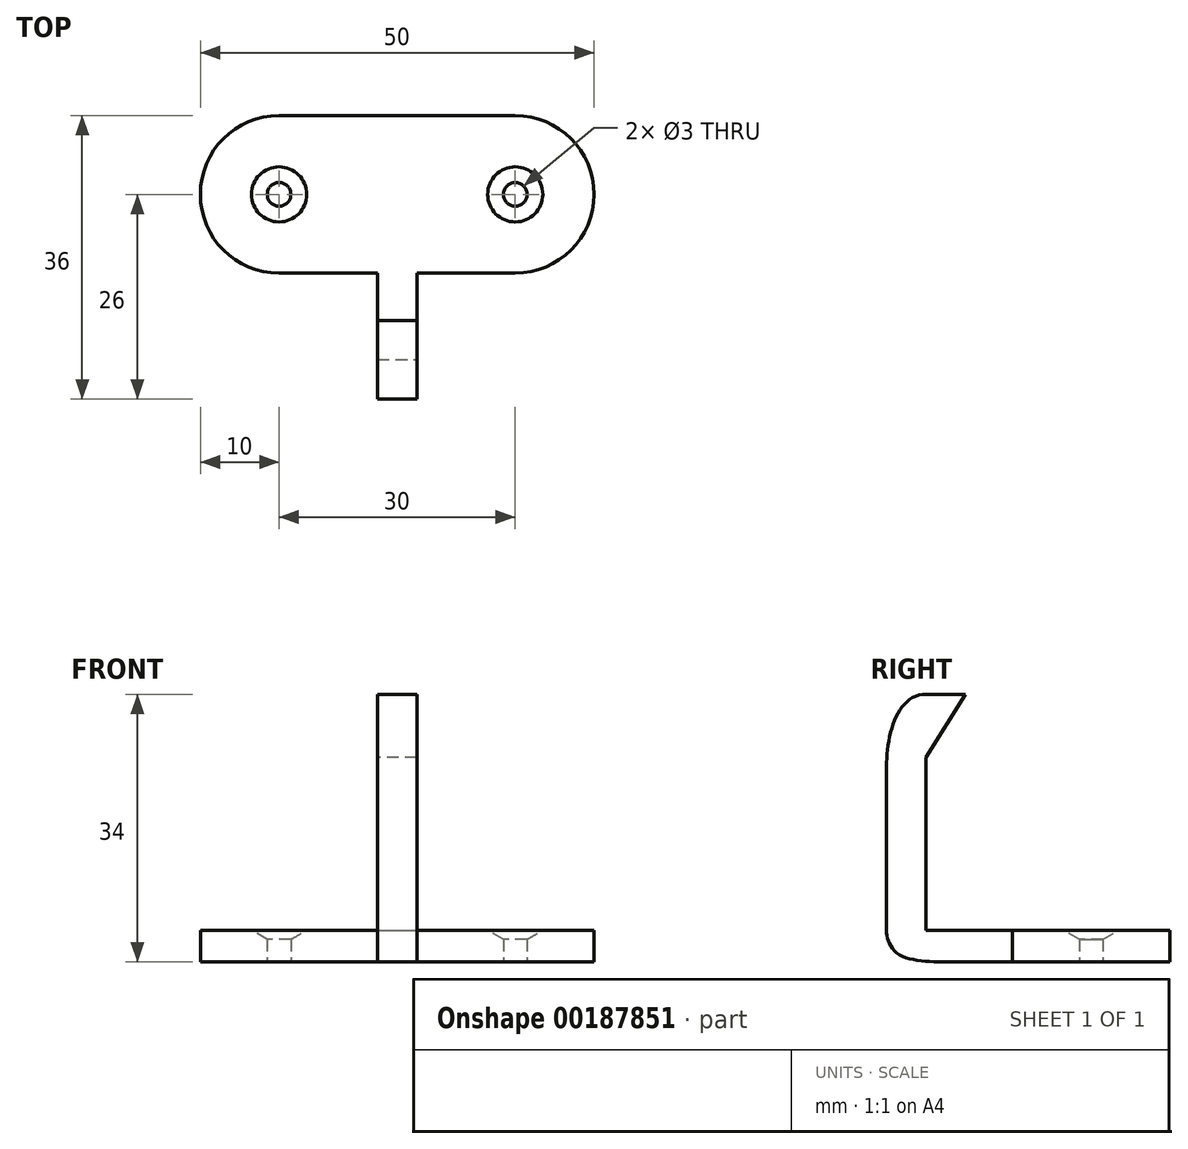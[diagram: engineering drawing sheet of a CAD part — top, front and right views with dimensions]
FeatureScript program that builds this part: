
annotation { "Feature Type Name" : "Feature", "Feature Type Description" : "" }
export const myFeature = defineFeature(function(context is Context, id is Id, definition is map)
    precondition{}
    {
        {
            var Q0;
            Q0=qCreatedBy(makeId("Top.planeOp"),FACE);
            var sketch = newSketch(context, id + "F0", { "sketchPlane" : qUnion([Q0])});
            skLineSegment(sketch, "E0.bottom", {"start": v(-15, 10) * mm, "end": v(15, 10) * mm});
            skLineSegment(sketch, "E0.top", {"start": v(-15, -10) * mm, "end": v(15, -10) * mm});
            skArc(sketch, "E1", {"start": v(-15, 10) * mm, "mid": v(-25, 0) * mm, "end": v(-15, -10) * mm});
            skArc(sketch, "E2", {"start": v(15, -10) * mm, "mid": v(25, 0) * mm, "end": v(15, 10) * mm});
            skPoint(sketch, "E2.centerSnap0", {"position": v(15, 0) * mm});
            skCircle(sketch, "E3", {"center": v(-15, 0) * mm, "radius": 1.5 * mm});
            skCircle(sketch, "E4", {"center": v(15, 0) * mm, "radius": 1.5 * mm});
            skSolve(sketch);
        }
        {
            var Q0;
            Q0=makeQuery(id+"F0.imprint","IMPRINT",FACE,{"disambiguationData":[TD([[makeQuery(id+"F0.imprint","IMPRINT",EDGE,{"derivedFrom":sQuery(id+"F0.wireOp",EDGE,"E0.bottom")}),-1.0]])]});
            extrude(context, id + "F1", {"entities" : qUnion([Q0]), "depth" : 4 * mm});
        }
        {
            var Q0;
            Q0=qCreatedBy(makeId("Right.planeOp"),FACE);
            var sketch = newSketch(context, id + "F2", { "sketchPlane" : qUnion([Q0])});
            skLineSegment(sketch, "E5.bottom", {"start": v(10, 4) * mm, "end": v(-10, 4) * mm});
            skLineSegment(sketch, "E5.top", {"start": v(10, 0) * mm, "end": v(-10, 0) * mm});
            skLineSegment(sketch, "E5.left", {"start": v(10, 4) * mm, "end": v(10, 0) * mm});
            skLineSegment(sketch, "E5.right", {"start": v(-10, 4) * mm, "end": v(-10, 0) * mm});
            skLineSegment(sketch, "E6.bottom", {"start": v(-10, 4) * mm, "end": v(-26, 4) * mm});
            skLineSegment(sketch, "E6.top", {"start": v(-10, 0) * mm, "end": v(-18, 0) * mm});
            skLineSegment(sketch, "E6.right", {"start": v(-26, 4) * mm, "end": v(-26, 3) * mm});
            skFitSpline(sketch, "E7", {"points": [v(-26, 4) * mm, v(-24.52, 1) * mm, v(-18, 0) * mm], "startDerivative": vector(0, -7.21) * mm, "endDerivative": vector(10.27, 0) * mm});
            skPoint(sketch, "E8.orphan", {"position": v(-26, 0) * mm});
            skSolve(sketch);
        }
        {
            var Q0;
            Q0=makeQuery(id+"F2.imprint","IMPRINT",FACE,{"disambiguationData":[TD([[makeQuery(id+"F2.imprint","IMPRINT",EDGE,{"derivedFrom":sQuery(id+"F2.wireOp",EDGE,"E6.bottom")}),1.0]])]});
            extrude(context, id + "F3", {"entities" : qUnion([Q0]), "operationType" : NewBodyOperationType.ADD, "endBound" : BoundingType.SYMMETRIC, "depth" : 5 * mm});
        }
        {
            var Q0;
            Q0=makeQuery(id+"F3.boolean.opBoolean","MERGE",FACE,{"derivedFrom":[makeQuery(id+"F1.opExtrude","CAP_FACE",FACE,{"disambiguationData":[OSD([sQuery(id+"F0.wireOp",EDGE,"E0.bottom"),sQuery(id+"F0.wireOp",EDGE,"E0.top"),sQuery(id+"F0.wireOp",EDGE,"E1"),sQuery(id+"F0.wireOp",EDGE,"E2"),sQuery(id+"F0.wireOp",EDGE,"E3"),sQuery(id+"F0.wireOp",EDGE,"E4")])],"isStart":false}),makeQuery(id+"F3.opExtrude","SWEPT_FACE",FACE,{"disambiguationData":[OSD([sQuery(id+"F2.wireOp",EDGE,"E6.bottom")])]})]});
            var sketch = newSketch(context, id + "F4", { "sketchPlane" : qUnion([Q0])});
            skLineSegment(sketch, "E9.bottom", {"start": v(-2.5, -26) * mm, "end": v(2.5, -26) * mm});
            skLineSegment(sketch, "E9.top", {"start": v(-2.5, -21) * mm, "end": v(2.5, -21) * mm});
            skLineSegment(sketch, "E9.left", {"start": v(-2.5, -26) * mm, "end": v(-2.5, -21) * mm});
            skLineSegment(sketch, "E9.right", {"start": v(2.5, -26) * mm, "end": v(2.5, -21) * mm});
            skSolve(sketch);
        }
        {
            var Q0;
            Q0=makeQuery(id+"F4.imprint","IMPRINT",FACE,{"disambiguationData":[TD([[makeQuery(id+"F4.imprint","IMPRINT",EDGE,{"derivedFrom":sQuery(id+"F4.wireOp",EDGE,"E9.bottom")}),-1.0]])]});
            extrude(context, id + "F5", {"entities" : qUnion([Q0]), "operationType" : NewBodyOperationType.ADD, "depth" : 30 * mm});
        }
        {
            var Q0;
            Q0=makeQuery(id+"F5.boolean.opBoolean","MERGE",FACE,{"derivedFrom":[makeQuery(id+"F3.opExtrude","CAP_FACE",FACE,{"disambiguationData":[OSD([sQuery(id+"F2.wireOp",EDGE,"E6.bottom"),sQuery(id+"F2.wireOp",EDGE,"E6.top"),sQuery(id+"F2.wireOp",EDGE,"E5.right"),sQuery(id+"F2.wireOp",EDGE,"E7")])],"isStart":true}),makeQuery(id+"F5.opExtrude","SWEPT_FACE",FACE,{"disambiguationData":[OSD([sQuery(id+"F4.wireOp",EDGE,"E9.left")])]})]});
            var sketch = newSketch(context, id + "F6", { "sketchPlane" : qUnion([Q0])});
            skFitSpline(sketch, "E10", {"points": [v(26, 24.79) * mm, v(21, 34) * mm], "startDerivative": vector(0, 11.97) * mm, "endDerivative": vector(-11.06, 0) * mm});
            skLineSegment(sketch, "E11", {"start": v(21, 34) * mm, "end": v(16, 34) * mm});
            skLineSegment(sketch, "E12", {"start": v(16, 34) * mm, "end": v(21, 26) * mm});
            skLineSegment(sketch, "E13", {"start": v(21, 26) * mm, "end": v(21, 34) * mm});
            skSolve(sketch);
        }
        {
            var Q0;
            {var subQ0=sQuery(id+"F6.wireOp",EDGE,"E10");Q0=makeQuery(id+"F6.imprint","IMPRINT",FACE,{"disambiguationData":[TD([[makeQuery(id+"F6.imprint","IMPRINT",EDGE,{"derivedFrom":subQ0}),-1.0]])]});}
            extrude(context, id + "F7", {"entities" : qUnion([Q0]), "operationType" : NewBodyOperationType.REMOVE, "endBound" : BoundingType.UP_TO_NEXT, "oppositeDirection" : true, "depth" : 25 * mm});
        }
        {
            var Q0;
            Q0=qCreatedBy(makeId("Right.planeOp"),FACE);
            var Q1;
            Q1=sQuery(id+"F0.wireOp",VERTEX,"E2.centerSnap0");
            cPlane(context, id + "F8", {"entities" : qUnion([Q0, Q1]), "cplaneType" : CPlaneType.PLANE_POINT, "offset" : 16 * mm, "width" : 150 * mm, "height" : 150 * mm});
        }
        {
            var Q0;
            Q0=qCreatedBy(id+"F8.planeOp",FACE);
            var sketch = newSketch(context, id + "F9", { "sketchPlane" : qUnion([Q0])});
            skLineSegment(sketch, "E14", {"start": v(0, 0) * mm, "end": v(0, 4) * mm, "construction": true});
            skLineSegment(sketch, "E15", {"start": v(0, 4) * mm, "end": v(3.5, 4) * mm});
            skLineSegment(sketch, "E16", {"start": v(0, 4) * mm, "end": v(-3.5, 4) * mm, "construction": true});
            skLineSegment(sketch, "E17", {"start": v(0, 2) * mm, "end": v(3.5, 4) * mm});
            skLineSegment(sketch, "E18", {"start": v(0, 4) * mm, "end": v(0, 2) * mm});
            skSolve(sketch);
        }
        {
            var Q0;
            Q0=makeQuery(id+"F9.imprint","IMPRINT",FACE,{"disambiguationData":[TD([[makeQuery(id+"F9.imprint","IMPRINT",EDGE,{"derivedFrom":sQuery(id+"F9.wireOp",EDGE,"E15")}),-1.0]])]});
            var Q1;
            Q1=sQuery(id+"F9.wireOp",EDGE,"E18");
            revolve(context, id + "F10", {"operationType" : NewBodyOperationType.REMOVE, "entities" : qUnion([Q0]), "axis" : qUnion([Q1]), "revolveType" : RevolveType.FULL, "oppositeDirection" : true});
        }
        {
            var Q0;
            Q0=sQuery(id+"F0.wireOp",VERTEX,"E1.center");
            var Q1;
            Q1=qCreatedBy(makeId("Right.planeOp"),FACE);
            cPlane(context, id + "F11", {"entities" : qUnion([Q0, Q1]), "cplaneType" : CPlaneType.PLANE_POINT, "offset" : 25 * mm, "width" : 150 * mm, "height" : 150 * mm});
        }
        {
            var Q0;
            Q0=qCreatedBy(id+"F11.planeOp",FACE);
            var sketch = newSketch(context, id + "F12", { "sketchPlane" : qUnion([Q0])});
            skLineSegment(sketch, "E19", {"start": v(0, 0) * mm, "end": v(0, 4) * mm, "construction": true});
            skLineSegment(sketch, "E20", {"start": v(0, 4) * mm, "end": v(3.5, 4) * mm});
            skLineSegment(sketch, "E21", {"start": v(0, 4) * mm, "end": v(-3.5, 4) * mm, "construction": true});
            skLineSegment(sketch, "E22", {"start": v(0, 2) * mm, "end": v(3.5, 4) * mm});
            skLineSegment(sketch, "E23", {"start": v(0, 4) * mm, "end": v(0, 2) * mm});
            skSolve(sketch);
        }
        {
            var Q0;
            Q0=makeQuery(id+"F12.imprint","IMPRINT",FACE,{"disambiguationData":[TD([[makeQuery(id+"F12.imprint","IMPRINT",EDGE,{"derivedFrom":sQuery(id+"F12.wireOp",EDGE,"E20")}),-1.0]])]});
            var Q1;
            Q1=makeQuery(id+"F1.opExtrude","SWEPT_FACE",FACE,{"disambiguationData":[OSD([sQuery(id+"F0.wireOp",EDGE,"E1")])]});
            revolve(context, id + "F13", {"operationType" : NewBodyOperationType.REMOVE, "entities" : qUnion([Q0]), "axis" : qUnion([Q1]), "revolveType" : RevolveType.FULL, "oppositeDirection" : true});
        }
        {
            var Q0;
            Q0=makeQuery(id+"F6.imprint","IMPRINT",FACE,{"disambiguationData":[TD([[makeQuery(id+"F6.imprint","IMPRINT",EDGE,{"derivedFrom":sQuery(id+"F6.wireOp",EDGE,"E11")}),1.0]])]});
            var Q1;
            Q1=makeQuery(id+"F5.boolean.opBoolean","MERGE",FACE,{"derivedFrom":[makeQuery(id+"F3.opExtrude","CAP_FACE",FACE,{"disambiguationData":[OSD([sQuery(id+"F2.wireOp",EDGE,"E6.bottom"),sQuery(id+"F2.wireOp",EDGE,"E6.top"),sQuery(id+"F2.wireOp",EDGE,"E5.right"),sQuery(id+"F2.wireOp",EDGE,"E7")])],"isStart":false}),makeQuery(id+"F5.opExtrude","SWEPT_FACE",FACE,{"disambiguationData":[OSD([sQuery(id+"F4.wireOp",EDGE,"E9.right")])]})]});
            extrude(context, id + "F14", {"entities" : qUnion([Q0]), "operationType" : NewBodyOperationType.ADD, "endBound" : BoundingType.UP_TO_SURFACE, "oppositeDirection" : true, "endBoundEntityFace" : qUnion([Q1]), "depth" : 25 * mm});
        }
    });
